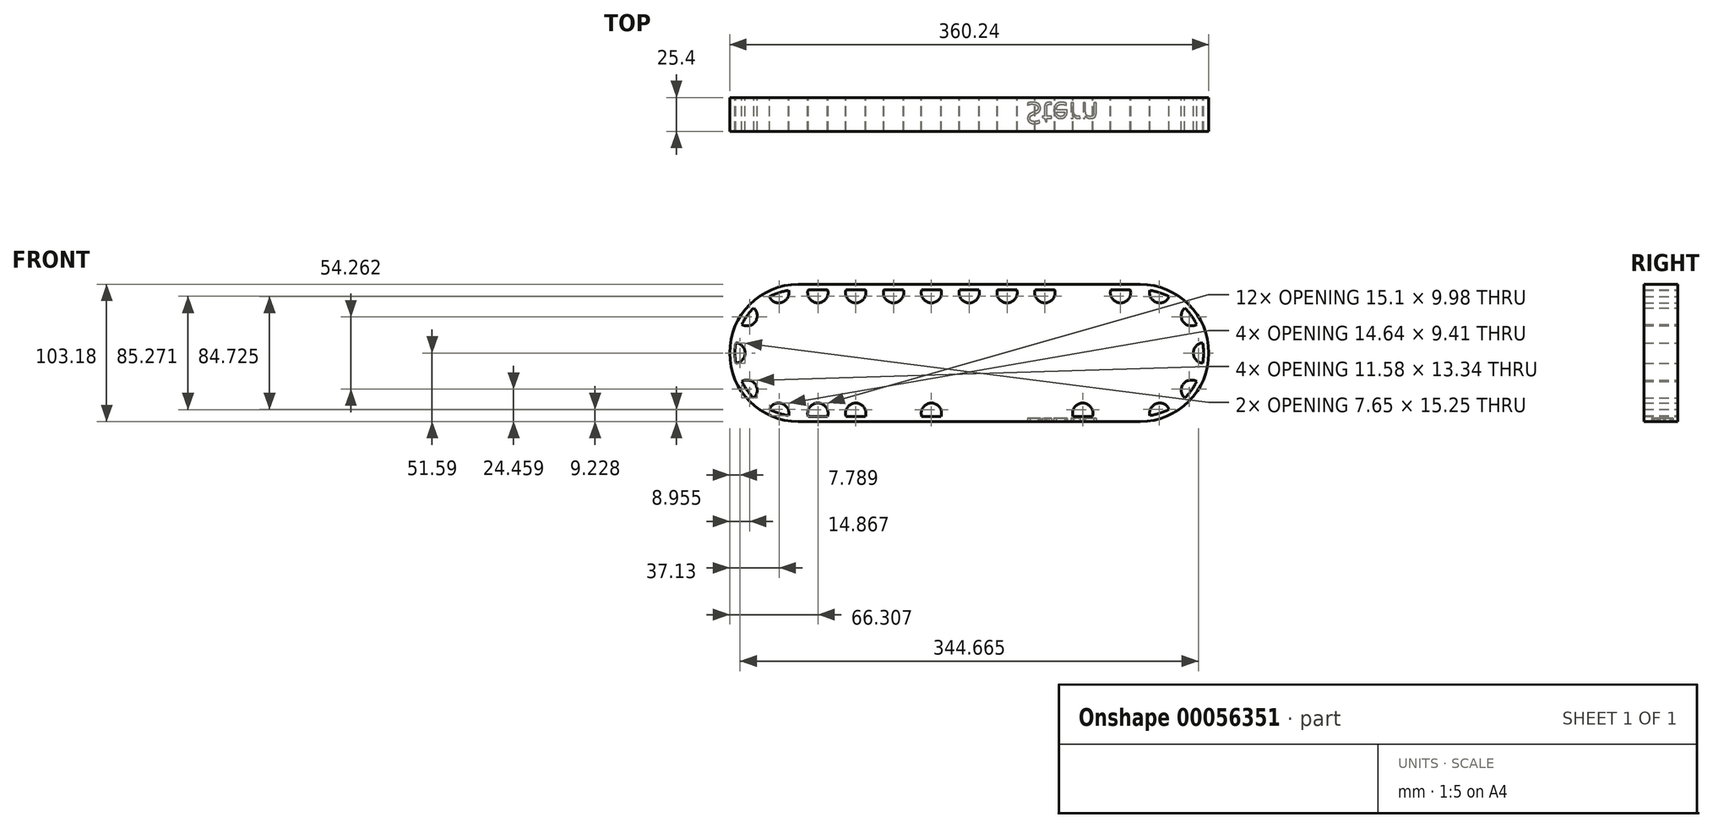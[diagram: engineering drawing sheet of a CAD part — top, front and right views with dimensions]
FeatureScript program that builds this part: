
annotation { "Feature Type Name" : "Feature", "Feature Type Description" : "" }
export const myFeature = defineFeature(function(context is Context, id is Id, definition is map)
    precondition{}
    {
        {
            var Q0;
            Q0=qCreatedBy(makeId("Front.planeOp"),FACE);
            var sketch = newSketch(context, id + "F0", { "sketchPlane" : qUnion([Q0])});
            skCircle(sketch, "E0", {"center": v(0, 0) * mm, "radius": 9.53 * mm});
            skCircle(sketch, "E1", {"center": v(0, 0) * mm, "radius": 15.88 * mm, "construction": true});
            skArc(sketch, "E2", {"start": v(15.06, 35) * mm, "mid": v(11.77, 36.24) * mm, "end": v(8.38, 37.17) * mm});
            skCircle(sketch, "E3", {"center": v(0, 0) * mm, "radius": 25.4 * mm});
            skArc(sketch, "E4", {"start": v(6.62, 47.16) * mm, "mid": v(0, 47.63) * mm, "end": v(-6.62, 47.16) * mm});
            skLineSegment(sketch, "E5", {"start": v(-6.62, 47.16) * mm, "end": v(-8.38, 37.17) * mm});
            skLineSegment(sketch, "E6", {"start": v(-8.38, 37.17) * mm, "end": v(8.38, 37.17) * mm, "construction": true});
            skLineSegment(sketch, "E7", {"start": v(8.38, 37.17) * mm, "end": v(6.62, 47.16) * mm});
            skLineSegment(sketch, "E8", {"start": v(0, 37.17) * mm, "end": v(0, 47.63) * mm, "construction": true});
            skPoint(sketch, "E8.endSnap0", {"position": v(0, 37.17) * mm});
            skArc(sketch, "E9.1.0", {"start": v(-22.36, 42.05) * mm, "mid": v(-28, 38.53) * mm, "end": v(-33.08, 34.26) * mm});
            skLineSegment(sketch, "E9.1.1", {"start": v(-33.08, 34.26) * mm, "end": v(-28.63, 25.14) * mm});
            skLineSegment(sketch, "E9.1.2", {"start": v(-15.06, 35) * mm, "end": v(-22.36, 42.05) * mm});
            skLineSegment(sketch, "E9.1.3", {"start": v(-28.63, 25.14) * mm, "end": v(-21.85, 30.07) * mm, "construction": true});
            skLineSegment(sketch, "E9.1.4", {"start": v(-21.85, 30.07) * mm, "end": v(-28, 38.53) * mm, "construction": true});
            skArc(sketch, "E9.2.0", {"start": v(-42.8, 20.87) * mm, "mid": v(-45.3, 14.72) * mm, "end": v(-46.9, 8.28) * mm});
            skLineSegment(sketch, "E9.2.1", {"start": v(-46.9, 8.28) * mm, "end": v(-37.94, 3.51) * mm});
            skLineSegment(sketch, "E9.2.2", {"start": v(-32.76, 19.46) * mm, "end": v(-42.8, 20.87) * mm});
            skLineSegment(sketch, "E9.2.3", {"start": v(-37.94, 3.51) * mm, "end": v(-32.76, 19.46) * mm, "construction": true});
            skLineSegment(sketch, "E9.2.4", {"start": v(-35.35, 11.48) * mm, "end": v(-45.3, 14.72) * mm, "construction": true});
            skArc(sketch, "E9.3.0", {"start": v(-46.9, -8.28) * mm, "mid": v(-45.3, -14.72) * mm, "end": v(-42.8, -20.87) * mm});
            skLineSegment(sketch, "E9.3.1", {"start": v(-42.8, -20.87) * mm, "end": v(-32.76, -19.46) * mm});
            skLineSegment(sketch, "E9.3.2", {"start": v(-37.94, -3.51) * mm, "end": v(-46.9, -8.28) * mm});
            skLineSegment(sketch, "E9.3.3", {"start": v(-32.76, -19.46) * mm, "end": v(-37.94, -3.51) * mm, "construction": true});
            skLineSegment(sketch, "E9.3.4", {"start": v(-35.35, -11.48) * mm, "end": v(-45.3, -14.72) * mm, "construction": true});
            skArc(sketch, "E9.4.0", {"start": v(-33.08, -34.26) * mm, "mid": v(-28, -38.53) * mm, "end": v(-22.36, -42.05) * mm});
            skLineSegment(sketch, "E9.4.1", {"start": v(-22.36, -42.05) * mm, "end": v(-15.06, -35) * mm});
            skLineSegment(sketch, "E9.4.2", {"start": v(-28.63, -25.14) * mm, "end": v(-33.08, -34.26) * mm});
            skLineSegment(sketch, "E9.4.3", {"start": v(-15.06, -35) * mm, "end": v(-28.63, -25.14) * mm, "construction": true});
            skLineSegment(sketch, "E9.4.4", {"start": v(-21.85, -30.07) * mm, "end": v(-28, -38.53) * mm, "construction": true});
            skArc(sketch, "E9.5.0", {"start": v(-6.62, -47.16) * mm, "mid": v(0, -47.63) * mm, "end": v(6.62, -47.16) * mm});
            skLineSegment(sketch, "E9.5.1", {"start": v(6.62, -47.16) * mm, "end": v(8.38, -37.17) * mm});
            skLineSegment(sketch, "E9.5.2", {"start": v(-8.38, -37.17) * mm, "end": v(-6.62, -47.16) * mm});
            skLineSegment(sketch, "E9.5.3", {"start": v(8.38, -37.17) * mm, "end": v(-8.38, -37.17) * mm, "construction": true});
            skLineSegment(sketch, "E9.5.4", {"start": v(0, -37.17) * mm, "end": v(0, -47.63) * mm, "construction": true});
            skArc(sketch, "E9.6.0", {"start": v(22.36, -42.05) * mm, "mid": v(28, -38.53) * mm, "end": v(33.08, -34.26) * mm});
            skLineSegment(sketch, "E9.6.1", {"start": v(33.08, -34.26) * mm, "end": v(28.63, -25.14) * mm});
            skLineSegment(sketch, "E9.6.2", {"start": v(15.06, -35) * mm, "end": v(22.36, -42.05) * mm});
            skLineSegment(sketch, "E9.6.3", {"start": v(28.63, -25.14) * mm, "end": v(15.06, -35) * mm, "construction": true});
            skLineSegment(sketch, "E9.6.4", {"start": v(21.85, -30.07) * mm, "end": v(28, -38.53) * mm, "construction": true});
            skArc(sketch, "E9.7.0", {"start": v(42.8, -20.87) * mm, "mid": v(45.3, -14.72) * mm, "end": v(46.9, -8.28) * mm});
            skLineSegment(sketch, "E9.7.1", {"start": v(46.9, -8.28) * mm, "end": v(37.94, -3.51) * mm});
            skLineSegment(sketch, "E9.7.2", {"start": v(32.76, -19.46) * mm, "end": v(42.8, -20.87) * mm});
            skLineSegment(sketch, "E9.7.3", {"start": v(37.94, -3.51) * mm, "end": v(32.76, -19.46) * mm, "construction": true});
            skLineSegment(sketch, "E9.7.4", {"start": v(35.35, -11.48) * mm, "end": v(45.3, -14.72) * mm, "construction": true});
            skArc(sketch, "E9.8.0", {"start": v(46.9, 8.28) * mm, "mid": v(45.3, 14.72) * mm, "end": v(42.8, 20.87) * mm});
            skLineSegment(sketch, "E9.8.1", {"start": v(42.8, 20.87) * mm, "end": v(32.76, 19.46) * mm});
            skLineSegment(sketch, "E9.8.2", {"start": v(37.94, 3.51) * mm, "end": v(46.9, 8.28) * mm});
            skLineSegment(sketch, "E9.8.3", {"start": v(32.76, 19.46) * mm, "end": v(37.94, 3.51) * mm, "construction": true});
            skLineSegment(sketch, "E9.8.4", {"start": v(35.35, 11.48) * mm, "end": v(45.3, 14.72) * mm, "construction": true});
            skArc(sketch, "E9.9.0", {"start": v(33.08, 34.26) * mm, "mid": v(28, 38.53) * mm, "end": v(22.36, 42.05) * mm});
            skLineSegment(sketch, "E9.9.1", {"start": v(22.36, 42.05) * mm, "end": v(15.06, 35) * mm});
            skLineSegment(sketch, "E9.9.2", {"start": v(28.63, 25.14) * mm, "end": v(33.08, 34.26) * mm});
            skLineSegment(sketch, "E9.9.3", {"start": v(15.06, 35) * mm, "end": v(28.63, 25.14) * mm, "construction": true});
            skLineSegment(sketch, "E9.9.4", {"start": v(21.85, 30.07) * mm, "end": v(28, 38.53) * mm, "construction": true});
            skArc(sketch, "E10.trimOffspring", {"start": v(37.94, -3.51) * mm, "mid": v(38.1, 0) * mm, "end": v(37.94, 3.51) * mm});
            skArc(sketch, "E11.trimOffspring", {"start": v(28.63, -25.14) * mm, "mid": v(30.82, -22.4) * mm, "end": v(32.76, -19.46) * mm});
            skArc(sketch, "E12.trimOffspring", {"start": v(8.38, -37.17) * mm, "mid": v(11.77, -36.24) * mm, "end": v(15.06, -35) * mm});
            skArc(sketch, "E13.trimOffspring", {"start": v(-15.06, -35) * mm, "mid": v(-11.77, -36.24) * mm, "end": v(-8.38, -37.17) * mm});
            skArc(sketch, "E14.trimOffspring", {"start": v(-32.76, -19.46) * mm, "mid": v(-30.82, -22.4) * mm, "end": v(-28.63, -25.14) * mm});
            skArc(sketch, "E15.trimOffspring", {"start": v(-37.94, 3.51) * mm, "mid": v(-38.1, 0) * mm, "end": v(-37.94, -3.51) * mm});
            skArc(sketch, "E16.trimOffspring", {"start": v(-8.38, 37.17) * mm, "mid": v(-11.77, 36.24) * mm, "end": v(-15.06, 35) * mm});
            skArc(sketch, "E17.trimOffspring", {"start": v(-28.63, 25.14) * mm, "mid": v(-29.76, 23.8) * mm, "end": v(-30.82, 22.4) * mm});
            skArc(sketch, "E18", {"start": v(-30.82, 22.4) * mm, "mid": v(-31.82, 20.95) * mm, "end": v(-32.76, 19.46) * mm});
            skArc(sketch, "E19.trimOffspring", {"start": v(32.76, 19.46) * mm, "mid": v(30.82, 22.4) * mm, "end": v(28.63, 25.14) * mm});
            skLineSegment(sketch, "E20", {"start": v(-21.85, 30.07) * mm, "end": v(-15.06, 35) * mm, "construction": true});
            skPoint(sketch, "E21.endSnap0", {"position": v(-30.82, 22.4) * mm});
            skLineSegment(sketch, "E22", {"start": v(0, 9.53) * mm, "end": v(0, 15.88) * mm, "construction": true});
            skLineSegment(sketch, "E23", {"start": v(0, 9.53) * mm, "end": v(0, 9.53) * mm});
            skLineSegment(sketch, "E24", {"start": v(-3.98, 8.66) * mm, "end": v(-3.98, 15.37) * mm, "construction": true});
            skLineSegment(sketch, "E25", {"start": v(3.98, 8.66) * mm, "end": v(3.98, 15.37) * mm, "construction": true});
            skLineSegment(sketch, "E26", {"start": v(3.98, 15.37) * mm, "end": v(3.98, 8.66) * mm, "construction": true});
            skLineSegment(sketch, "E27", {"start": v(3.98, 8.66) * mm, "end": v(-3.98, 8.66) * mm, "construction": true});
            skLineSegment(sketch, "E28", {"start": v(-3.98, 8.66) * mm, "end": v(-3.98, 25.09) * mm, "construction": true});
            skLineSegment(sketch, "E29", {"start": v(3.98, 8.66) * mm, "end": v(3.98, 25.09) * mm, "construction": true});
            skLineSegment(sketch, "E30", {"start": v(0, 9.53) * mm, "end": v(0, 25.4) * mm, "construction": true});
            skPoint(sketch, "E30.endSnap0", {"position": v(0, 12.7) * mm});
            skLineSegment(sketch, "E31.1.0", {"start": v(-9.48, -0.89) * mm, "end": v(-23.71, -9.1) * mm, "construction": true});
            skLineSegment(sketch, "E31.1.1", {"start": v(-8.25, -4.76) * mm, "end": v(-22, -12.7) * mm, "construction": true});
            skLineSegment(sketch, "E31.1.2", {"start": v(-5.5, -7.77) * mm, "end": v(-19.74, -15.99) * mm, "construction": true});
            skLineSegment(sketch, "E31.1.3", {"start": v(-9.48, -0.89) * mm, "end": v(-5.5, -7.77) * mm, "construction": true});
            skLineSegment(sketch, "E31.2.0", {"start": v(5.5, -7.77) * mm, "end": v(19.74, -15.99) * mm, "construction": true});
            skLineSegment(sketch, "E31.2.1", {"start": v(8.25, -4.76) * mm, "end": v(22, -12.7) * mm, "construction": true});
            skLineSegment(sketch, "E31.2.2", {"start": v(9.48, -0.89) * mm, "end": v(23.71, -9.1) * mm, "construction": true});
            skLineSegment(sketch, "E31.2.3", {"start": v(5.5, -7.77) * mm, "end": v(9.48, -0.89) * mm, "construction": true});
            skSolve(sketch);
        }
        {
            var Q0;
            Q0=qCreatedBy(makeId("Front.planeOp"),FACE);
            var sketch = newSketch(context, id + "F1", { "sketchPlane" : qUnion([Q0])});
            skArc(sketch, "E32", {"start": v(22.36, 42.05) * mm, "mid": v(22.07, 42.2) * mm, "end": v(21.78, 42.35) * mm});
            skLineSegment(sketch, "E33.0", {"start": v(22.36, 42.05) * mm, "end": v(15.06, 35) * mm, "construction": true});
            skLineSegment(sketch, "E33.1", {"start": v(8.38, 37.17) * mm, "end": v(6.62, 47.16) * mm, "construction": true});
            skLineSegment(sketch, "E33.2", {"start": v(-6.62, 47.16) * mm, "end": v(-8.38, 37.17) * mm, "construction": true});
            skLineSegment(sketch, "E33.3", {"start": v(-15.06, 35) * mm, "end": v(-22.36, 42.05) * mm, "construction": true});
            skLineSegment(sketch, "E33.4", {"start": v(-33.08, 34.26) * mm, "end": v(-28.63, 25.14) * mm, "construction": true});
            skLineSegment(sketch, "E33.5", {"start": v(-32.76, 19.46) * mm, "end": v(-42.8, 20.87) * mm, "construction": true});
            skLineSegment(sketch, "E33.6", {"start": v(-46.9, 8.28) * mm, "end": v(-37.94, 3.51) * mm, "construction": true});
            skLineSegment(sketch, "E33.7", {"start": v(-37.94, -3.51) * mm, "end": v(-46.9, -8.28) * mm, "construction": true});
            skLineSegment(sketch, "E33.8", {"start": v(-42.8, -20.87) * mm, "end": v(-32.76, -19.46) * mm, "construction": true});
            skCircle(sketch, "E34", {"center": v(-14.72, 45.3) * mm, "radius": 7.65 * mm});
            skCircle(sketch, "E35", {"center": v(-38.53, 28) * mm, "radius": 7.65 * mm});
            skCircle(sketch, "E36", {"center": v(-47.63, 0) * mm, "radius": 7.65 * mm});
            skCircle(sketch, "E37", {"center": v(-38.53, -28) * mm, "radius": 7.65 * mm});
            skCircle(sketch, "E38.MirrorC", {"center": v(14.72, 45.3) * mm, "radius": 7.65 * mm});
            skLineSegment(sketch, "E39", {"start": v(-14.72, 45.3) * mm, "end": v(14.72, 45.3) * mm, "construction": true});
            skArc(sketch, "E40.trimOffspring", {"start": v(-22.36, 42.05) * mm, "mid": v(-42.05, -22.36) * mm, "end": v(22.36, -42.05) * mm});
            skArc(sketch, "E41.trimOffspring", {"start": v(7.28, 47.07) * mm, "mid": v(0.33, 47.62) * mm, "end": v(-6.62, 47.16) * mm});
            skLineSegment(sketch, "E42", {"start": v(14.72, 45.3) * mm, "end": v(43.17, 45.3) * mm, "construction": true});
            skLineSegment(sketch, "E43", {"start": v(43.17, 45.3) * mm, "end": v(71.62, 45.3) * mm, "construction": true});
            skLineSegment(sketch, "E44", {"start": v(71.62, 45.3) * mm, "end": v(100.08, 45.3) * mm, "construction": true});
            skLineSegment(sketch, "E45", {"start": v(100.08, 45.3) * mm, "end": v(128.53, 45.3) * mm, "construction": true});
            skCircle(sketch, "E46", {"center": v(43.17, 45.3) * mm, "radius": 7.65 * mm});
            skCircle(sketch, "E47", {"center": v(71.62, 45.3) * mm, "radius": 7.65 * mm});
            skCircle(sketch, "E48", {"center": v(100.08, 45.3) * mm, "radius": 7.65 * mm});
            skCircle(sketch, "E49", {"center": v(128.53, 45.3) * mm, "radius": 7.65 * mm});
            skPoint(sketch, "E50", {"position": v(35.52, 45.3) * mm});
            skPoint(sketch, "E51", {"position": v(22.37, 45.3) * mm});
            skPoint(sketch, "E51.positionSnap0", {"position": v(28.94, 45.3) * mm});
            skLineSegment(sketch, "E52", {"start": v(0, 0) * mm, "end": v(128.53, 0) * mm, "construction": true});
            skLineSegment(sketch, "E53", {"start": v(128.53, 0) * mm, "end": v(128.53, 45.3) * mm, "construction": true});
            skCircle(sketch, "E54.MirrorC", {"center": v(43.17, -45.3) * mm, "radius": 7.65 * mm});
            skCircle(sketch, "E55.MirrorC", {"center": v(71.62, -45.3) * mm, "radius": 7.65 * mm});
            skCircle(sketch, "E56.MirrorC", {"center": v(100.08, -45.3) * mm, "radius": 7.65 * mm});
            skCircle(sketch, "E57.MirrorC", {"center": v(128.53, -45.3) * mm, "radius": 7.65 * mm});
            skCircle(sketch, "E58.MirrorC", {"center": v(14.72, -45.3) * mm, "radius": 7.65 * mm});
            skCircle(sketch, "E59.MirrorC", {"center": v(-14.72, -45.3) * mm, "radius": 7.65 * mm});
            skCircle(sketch, "E60.MirrorC", {"center": v(156.99, 45.3) * mm, "radius": 7.65 * mm});
            skCircle(sketch, "E61.MirrorC", {"center": v(185.44, 45.3) * mm, "radius": 7.65 * mm});
            skCircle(sketch, "E62.MirrorC", {"center": v(213.9, 45.3) * mm, "radius": 7.65 * mm});
            skCircle(sketch, "E63.MirrorC", {"center": v(242.35, 45.3) * mm, "radius": 7.65 * mm});
            skCircle(sketch, "E64.MirrorC", {"center": v(271.78, 45.3) * mm, "radius": 7.65 * mm});
            skCircle(sketch, "E65.MirrorC", {"center": v(295.6, 28) * mm, "radius": 7.65 * mm});
            skCircle(sketch, "E66.MirrorC", {"center": v(304.69, 0) * mm, "radius": 7.65 * mm});
            skCircle(sketch, "E67.MirrorC", {"center": v(295.6, -28) * mm, "radius": 7.65 * mm});
            skCircle(sketch, "E68.MirrorC", {"center": v(271.78, -45.3) * mm, "radius": 7.65 * mm});
            skCircle(sketch, "E69.MirrorC", {"center": v(242.35, -45.3) * mm, "radius": 7.65 * mm});
            skCircle(sketch, "E70.MirrorC", {"center": v(213.9, -45.3) * mm, "radius": 7.65 * mm});
            skCircle(sketch, "E71.MirrorC", {"center": v(185.44, -45.3) * mm, "radius": 7.65 * mm});
            skCircle(sketch, "E72.MirrorC", {"center": v(156.99, -45.3) * mm, "radius": 7.65 * mm});
            skSolve(sketch);
        }
        {
            var Q0;
            Q0=qCreatedBy(makeId("Front.planeOp"),FACE);
            var sketch = newSketch(context, id + "F2", { "sketchPlane" : qUnion([Q0])});
            skArc(sketch, "E73", {"start": v(0, -47.63) * mm, "mid": v(-47.63, 0) * mm, "end": v(0, 47.63) * mm});
            skLineSegment(sketch, "E74", {"start": v(0, 47.63) * mm, "end": v(257.06, 47.63) * mm});
            skLineSegment(sketch, "E75", {"start": v(0, -47.63) * mm, "end": v(257.06, -47.62) * mm});
            skLineSegment(sketch, "E76.0", {"start": v(128.53, 0) * mm, "end": v(128.53, 45.3) * mm, "construction": true});
            skLineSegment(sketch, "E77.0", {"start": v(0, 0) * mm, "end": v(128.53, 0) * mm, "construction": true});
            skLineSegment(sketch, "E78.MirrorCS", {"start": v(257.06, 0) * mm, "end": v(128.53, 0) * mm, "construction": true});
            skArc(sketch, "E79", {"start": v(257.06, 47.63) * mm, "mid": v(304.69, 0) * mm, "end": v(257.06, -47.63) * mm});
            skLineSegment(sketch, "E80.0", {"start": v(0, 51.59) * mm, "end": v(257.06, 51.59) * mm});
            skArc(sketch, "E80.1", {"start": v(0, -51.59) * mm, "mid": v(-51.59, 0) * mm, "end": v(0, 51.59) * mm});
            skLineSegment(sketch, "E80.2", {"start": v(0, -51.59) * mm, "end": v(257.06, -51.59) * mm});
            skArc(sketch, "E80.3", {"start": v(257.06, 51.59) * mm, "mid": v(308.65, 0) * mm, "end": v(257.06, -51.59) * mm});
            skArc(sketch, "E81.0", {"start": v(19.06, 51.59) * mm, "mid": v(14.72, 37.65) * mm, "end": v(10.37, 51.59) * mm});
            skArc(sketch, "E81.1", {"start": v(-22.26, 46.54) * mm, "mid": v(-12.35, 38.02) * mm, "end": v(-9.34, 50.73) * mm});
            skArc(sketch, "E81.2", {"start": v(38.82, 51.59) * mm, "mid": v(43.17, 37.65) * mm, "end": v(47.52, 51.59) * mm});
            skArc(sketch, "E81.3", {"start": v(67.28, 51.59) * mm, "mid": v(71.62, 37.65) * mm, "end": v(75.97, 51.59) * mm});
            skArc(sketch, "E81.4", {"start": v(95.73, 51.59) * mm, "mid": v(100.08, 37.65) * mm, "end": v(104.42, 51.59) * mm});
            skArc(sketch, "E81.5", {"start": v(132.88, 51.59) * mm, "mid": v(128.53, 37.65) * mm, "end": v(124.19, 51.59) * mm});
            skArc(sketch, "E81.6", {"start": v(161.33, 51.59) * mm, "mid": v(159.45, 38.05) * mm, "end": v(149.7, 47.63) * mm});
            skArc(sketch, "E81.7", {"start": v(189.79, 51.59) * mm, "mid": v(185.44, 37.65) * mm, "end": v(181.1, 51.59) * mm});
            skArc(sketch, "E81.8", {"start": v(218.24, 51.59) * mm, "mid": v(213.9, 37.65) * mm, "end": v(209.55, 51.59) * mm});
            skArc(sketch, "E81.9", {"start": v(238, 51.59) * mm, "mid": v(242.35, 37.65) * mm, "end": v(246.7, 51.59) * mm});
            skArc(sketch, "E81.10", {"start": v(218.24, -51.59) * mm, "mid": v(213.9, -37.65) * mm, "end": v(209.55, -51.59) * mm});
            skArc(sketch, "E81.11", {"start": v(189.79, -51.59) * mm, "mid": v(185.44, -37.65) * mm, "end": v(181.1, -51.59) * mm});
            skArc(sketch, "E81.12", {"start": v(161.33, -51.59) * mm, "mid": v(156.99, -37.65) * mm, "end": v(152.64, -51.59) * mm});
            skArc(sketch, "E81.13", {"start": v(124.19, -51.59) * mm, "mid": v(128.53, -37.65) * mm, "end": v(132.88, -51.59) * mm});
            skArc(sketch, "E81.14", {"start": v(95.73, -51.59) * mm, "mid": v(100.08, -37.65) * mm, "end": v(104.42, -51.59) * mm});
            skArc(sketch, "E81.15", {"start": v(67.28, -51.59) * mm, "mid": v(71.62, -37.65) * mm, "end": v(75.97, -51.59) * mm});
            skArc(sketch, "E81.16", {"start": v(38.82, -51.59) * mm, "mid": v(43.17, -37.65) * mm, "end": v(47.52, -51.59) * mm});
            skArc(sketch, "E81.17", {"start": v(-45.36, 24.56) * mm, "mid": v(-32.34, 23.5) * mm, "end": v(-37.38, 35.55) * mm});
            skArc(sketch, "E81.18", {"start": v(-51.14, -6.8) * mm, "mid": v(-39.98, 0) * mm, "end": v(-51.14, 6.8) * mm});
            skArc(sketch, "E81.19", {"start": v(-45.36, -24.56) * mm, "mid": v(-32.34, -23.5) * mm, "end": v(-37.38, -35.55) * mm});
            skArc(sketch, "E81.20", {"start": v(-22.26, -46.54) * mm, "mid": v(-12.35, -38.02) * mm, "end": v(-9.34, -50.73) * mm});
            skArc(sketch, "E81.21", {"start": v(19.06, -51.59) * mm, "mid": v(14.72, -37.65) * mm, "end": v(10.37, -51.59) * mm});
            skArc(sketch, "E81.22", {"start": v(238, -51.59) * mm, "mid": v(242.35, -37.65) * mm, "end": v(246.7, -51.59) * mm});
            skArc(sketch, "E81.23", {"start": v(279.33, -46.54) * mm, "mid": v(269.42, -38.02) * mm, "end": v(266.4, -50.73) * mm});
            skArc(sketch, "E81.24", {"start": v(302.43, -24.56) * mm, "mid": v(289.4, -23.5) * mm, "end": v(294.44, -35.55) * mm});
            skArc(sketch, "E81.25", {"start": v(308.2, -6.8) * mm, "mid": v(297.04, 0) * mm, "end": v(308.2, 6.8) * mm});
            skArc(sketch, "E81.26", {"start": v(302.43, 24.56) * mm, "mid": v(289.4, 23.5) * mm, "end": v(294.44, 35.55) * mm});
            skArc(sketch, "E81.27", {"start": v(279.33, 46.54) * mm, "mid": v(269.42, 38.02) * mm, "end": v(266.4, 50.73) * mm});
            skSolve(sketch);
        }
        {
            var Q0;
            Q0 = qSketchRegion(id + "F2", true);
            var Q1;
            {var subQ0=sQuery(id+"F2.wireOp",EDGE,"E81.20");var subQ1=sQuery(id+"F2.wireOp",EDGE,"E73");var subQ2=makeQuery(id+"F2.imprint","INTERSECT",VERTEX,{"disambiguationData":[OD(0.0)],"derivedFrom":[subQ1,subQ0]});Q1=makeQuery(id+"F2.imprint","IMPRINT",FACE,{"disambiguationData":[TD([[makeQuery(id+"F2.imprint","IMPRINT",EDGE,{"disambiguationData":[TD([[subQ2,-1.0]])],"derivedFrom":subQ1}),-1.0]])]});}
            var Q2;
            {var subQ0=sQuery(id+"F2.wireOp",EDGE,"E81.21");var subQ1=sQuery(id+"F2.wireOp",EDGE,"E75");var subQ2=makeQuery(id+"F2.imprint","INTERSECT",VERTEX,{"disambiguationData":[OD(0.0)],"derivedFrom":[subQ1,subQ0]});Q2=makeQuery(id+"F2.imprint","IMPRINT",FACE,{"disambiguationData":[TD([[makeQuery(id+"F2.imprint","IMPRINT",EDGE,{"disambiguationData":[TD([[subQ2,-1.0]])],"derivedFrom":subQ1}),1.0]])]});}
            var Q3;
            {var subQ0=sQuery(id+"F2.wireOp",EDGE,"E81.16");var subQ1=sQuery(id+"F2.wireOp",EDGE,"E75");var subQ2=makeQuery(id+"F2.imprint","INTERSECT",VERTEX,{"disambiguationData":[OD(0.0)],"derivedFrom":[subQ1,subQ0]});Q3=makeQuery(id+"F2.imprint","IMPRINT",FACE,{"disambiguationData":[TD([[makeQuery(id+"F2.imprint","IMPRINT",EDGE,{"disambiguationData":[TD([[subQ2,-1.0]])],"derivedFrom":subQ1}),1.0]])]});}
            var Q4;
            {var subQ0=sQuery(id+"F2.wireOp",EDGE,"E81.15");var subQ1=sQuery(id+"F2.wireOp",EDGE,"E75");var subQ2=makeQuery(id+"F2.imprint","INTERSECT",VERTEX,{"disambiguationData":[OD(0.0)],"derivedFrom":[subQ1,subQ0]});Q4=makeQuery(id+"F2.imprint","IMPRINT",FACE,{"disambiguationData":[TD([[makeQuery(id+"F2.imprint","IMPRINT",EDGE,{"disambiguationData":[TD([[subQ2,-1.0]])],"derivedFrom":subQ1}),1.0]])]});}
            var Q5;
            {var subQ0=sQuery(id+"F2.wireOp",EDGE,"E81.14");var subQ1=sQuery(id+"F2.wireOp",EDGE,"E75");var subQ2=makeQuery(id+"F2.imprint","INTERSECT",VERTEX,{"disambiguationData":[OD(0.0)],"derivedFrom":[subQ1,subQ0]});Q5=makeQuery(id+"F2.imprint","IMPRINT",FACE,{"disambiguationData":[TD([[makeQuery(id+"F2.imprint","IMPRINT",EDGE,{"disambiguationData":[TD([[subQ2,-1.0]])],"derivedFrom":subQ1}),1.0]])]});}
            var Q6;
            {var subQ0=sQuery(id+"F2.wireOp",EDGE,"E81.13");var subQ1=sQuery(id+"F2.wireOp",EDGE,"E75");var subQ2=makeQuery(id+"F2.imprint","INTERSECT",VERTEX,{"disambiguationData":[OD(0.0)],"derivedFrom":[subQ1,subQ0]});Q6=makeQuery(id+"F2.imprint","IMPRINT",FACE,{"disambiguationData":[TD([[makeQuery(id+"F2.imprint","IMPRINT",EDGE,{"disambiguationData":[TD([[subQ2,-1.0]])],"derivedFrom":subQ1}),1.0]])]});}
            var Q7;
            {var subQ0=sQuery(id+"F2.wireOp",EDGE,"E81.12");var subQ1=sQuery(id+"F2.wireOp",EDGE,"E75");var subQ2=makeQuery(id+"F2.imprint","INTERSECT",VERTEX,{"disambiguationData":[OD(0.0)],"derivedFrom":[subQ1,subQ0]});Q7=makeQuery(id+"F2.imprint","IMPRINT",FACE,{"disambiguationData":[TD([[makeQuery(id+"F2.imprint","IMPRINT",EDGE,{"disambiguationData":[TD([[subQ2,-1.0]])],"derivedFrom":subQ1}),1.0]])]});}
            var Q8;
            {var subQ0=sQuery(id+"F2.wireOp",EDGE,"E81.11");var subQ1=sQuery(id+"F2.wireOp",EDGE,"E75");var subQ2=makeQuery(id+"F2.imprint","INTERSECT",VERTEX,{"disambiguationData":[OD(0.0)],"derivedFrom":[subQ1,subQ0]});Q8=makeQuery(id+"F2.imprint","IMPRINT",FACE,{"disambiguationData":[TD([[makeQuery(id+"F2.imprint","IMPRINT",EDGE,{"disambiguationData":[TD([[subQ2,-1.0]])],"derivedFrom":subQ1}),1.0]])]});}
            var Q9;
            {var subQ0=sQuery(id+"F2.wireOp",EDGE,"E81.10");var subQ1=sQuery(id+"F2.wireOp",EDGE,"E75");var subQ2=makeQuery(id+"F2.imprint","INTERSECT",VERTEX,{"disambiguationData":[OD(0.0)],"derivedFrom":[subQ1,subQ0]});Q9=makeQuery(id+"F2.imprint","IMPRINT",FACE,{"disambiguationData":[TD([[makeQuery(id+"F2.imprint","IMPRINT",EDGE,{"disambiguationData":[TD([[subQ2,-1.0]])],"derivedFrom":subQ1}),1.0]])]});}
            var Q10;
            {var subQ0=sQuery(id+"F2.wireOp",EDGE,"E81.22");var subQ1=sQuery(id+"F2.wireOp",EDGE,"E75");var subQ2=makeQuery(id+"F2.imprint","INTERSECT",VERTEX,{"disambiguationData":[OD(0.0)],"derivedFrom":[subQ1,subQ0]});Q10=makeQuery(id+"F2.imprint","IMPRINT",FACE,{"disambiguationData":[TD([[makeQuery(id+"F2.imprint","IMPRINT",EDGE,{"disambiguationData":[TD([[subQ2,-1.0]])],"derivedFrom":subQ1}),1.0]])]});}
            var Q11;
            {var subQ0=sQuery(id+"F2.wireOp",EDGE,"E81.23");var subQ1=sQuery(id+"F2.wireOp",EDGE,"E79");var subQ2=makeQuery(id+"F2.imprint","INTERSECT",VERTEX,{"disambiguationData":[OD(0.0)],"derivedFrom":[subQ1,subQ0]});Q11=makeQuery(id+"F2.imprint","IMPRINT",FACE,{"disambiguationData":[TD([[makeQuery(id+"F2.imprint","IMPRINT",EDGE,{"disambiguationData":[TD([[subQ2,-1.0]])],"derivedFrom":subQ1}),-1.0]])]});}
            var Q12;
            {var subQ0=sQuery(id+"F2.wireOp",EDGE,"E81.0");var subQ1=sQuery(id+"F2.wireOp",EDGE,"E74");var subQ2=makeQuery(id+"F2.imprint","INTERSECT",VERTEX,{"disambiguationData":[OD(0.0)],"derivedFrom":[subQ1,subQ0]});Q12=makeQuery(id+"F2.imprint","IMPRINT",FACE,{"disambiguationData":[TD([[makeQuery(id+"F2.imprint","IMPRINT",EDGE,{"disambiguationData":[TD([[subQ2,-1.0]])],"derivedFrom":subQ1}),-1.0]])]});}
            var Q13;
            {var subQ0=sQuery(id+"F2.wireOp",EDGE,"E81.1");var subQ1=sQuery(id+"F2.wireOp",EDGE,"E73");var subQ2=makeQuery(id+"F2.imprint","INTERSECT",VERTEX,{"disambiguationData":[OD(0.0)],"derivedFrom":[subQ1,subQ0]});Q13=makeQuery(id+"F2.imprint","IMPRINT",FACE,{"disambiguationData":[TD([[makeQuery(id+"F2.imprint","IMPRINT",EDGE,{"disambiguationData":[TD([[subQ2,-1.0]])],"derivedFrom":subQ1}),-1.0]])]});}
            var Q14;
            {var subQ0=sQuery(id+"F2.wireOp",EDGE,"E81.17");var subQ1=sQuery(id+"F2.wireOp",EDGE,"E73");var subQ2=makeQuery(id+"F2.imprint","INTERSECT",VERTEX,{"disambiguationData":[OD(0.0)],"derivedFrom":[subQ1,subQ0]});Q14=makeQuery(id+"F2.imprint","IMPRINT",FACE,{"disambiguationData":[TD([[makeQuery(id+"F2.imprint","IMPRINT",EDGE,{"disambiguationData":[TD([[subQ2,-1.0]])],"derivedFrom":subQ1}),-1.0]])]});}
            var Q15;
            {var subQ0=sQuery(id+"F2.wireOp",EDGE,"E81.18");var subQ1=sQuery(id+"F2.wireOp",EDGE,"E73");var subQ2=makeQuery(id+"F2.imprint","INTERSECT",VERTEX,{"disambiguationData":[OD(0.0)],"derivedFrom":[subQ1,subQ0]});Q15=makeQuery(id+"F2.imprint","IMPRINT",FACE,{"disambiguationData":[TD([[makeQuery(id+"F2.imprint","IMPRINT",EDGE,{"disambiguationData":[TD([[subQ2,-1.0]])],"derivedFrom":subQ1}),-1.0]])]});}
            var Q16;
            {var subQ0=sQuery(id+"F2.wireOp",EDGE,"E81.19");var subQ1=sQuery(id+"F2.wireOp",EDGE,"E73");var subQ2=makeQuery(id+"F2.imprint","INTERSECT",VERTEX,{"disambiguationData":[OD(0.0)],"derivedFrom":[subQ1,subQ0]});Q16=makeQuery(id+"F2.imprint","IMPRINT",FACE,{"disambiguationData":[TD([[makeQuery(id+"F2.imprint","IMPRINT",EDGE,{"disambiguationData":[TD([[subQ2,-1.0]])],"derivedFrom":subQ1}),-1.0]])]});}
            var Q17;
            {var subQ0=sQuery(id+"F2.wireOp",EDGE,"E81.2");var subQ1=sQuery(id+"F2.wireOp",EDGE,"E74");var subQ2=makeQuery(id+"F2.imprint","INTERSECT",VERTEX,{"disambiguationData":[OD(0.0)],"derivedFrom":[subQ1,subQ0]});Q17=makeQuery(id+"F2.imprint","IMPRINT",FACE,{"disambiguationData":[TD([[makeQuery(id+"F2.imprint","IMPRINT",EDGE,{"disambiguationData":[TD([[subQ2,-1.0]])],"derivedFrom":subQ1}),-1.0]])]});}
            var Q18;
            {var subQ0=sQuery(id+"F2.wireOp",EDGE,"E81.3");var subQ1=sQuery(id+"F2.wireOp",EDGE,"E74");var subQ2=makeQuery(id+"F2.imprint","INTERSECT",VERTEX,{"disambiguationData":[OD(0.0)],"derivedFrom":[subQ1,subQ0]});Q18=makeQuery(id+"F2.imprint","IMPRINT",FACE,{"disambiguationData":[TD([[makeQuery(id+"F2.imprint","IMPRINT",EDGE,{"disambiguationData":[TD([[subQ2,-1.0]])],"derivedFrom":subQ1}),-1.0]])]});}
            var Q19;
            {var subQ0=sQuery(id+"F2.wireOp",EDGE,"E81.4");var subQ1=sQuery(id+"F2.wireOp",EDGE,"E74");var subQ2=makeQuery(id+"F2.imprint","INTERSECT",VERTEX,{"disambiguationData":[OD(0.0)],"derivedFrom":[subQ1,subQ0]});Q19=makeQuery(id+"F2.imprint","IMPRINT",FACE,{"disambiguationData":[TD([[makeQuery(id+"F2.imprint","IMPRINT",EDGE,{"disambiguationData":[TD([[subQ2,-1.0]])],"derivedFrom":subQ1}),-1.0]])]});}
            var Q20;
            {var subQ0=sQuery(id+"F2.wireOp",EDGE,"E81.5");var subQ1=sQuery(id+"F2.wireOp",EDGE,"E74");var subQ2=makeQuery(id+"F2.imprint","INTERSECT",VERTEX,{"disambiguationData":[OD(0.0)],"derivedFrom":[subQ1,subQ0]});Q20=makeQuery(id+"F2.imprint","IMPRINT",FACE,{"disambiguationData":[TD([[makeQuery(id+"F2.imprint","IMPRINT",EDGE,{"disambiguationData":[TD([[subQ2,-1.0]])],"derivedFrom":subQ1}),-1.0]])]});}
            var Q21;
            {var subQ0=sQuery(id+"F2.wireOp",EDGE,"E81.6");var subQ1=sQuery(id+"F2.wireOp",EDGE,"E74");var subQ2=makeQuery(id+"F2.imprint","INTERSECT",VERTEX,{"disambiguationData":[OD(0.0)],"derivedFrom":[subQ1,subQ0]});Q21=makeQuery(id+"F2.imprint","IMPRINT",FACE,{"disambiguationData":[TD([[makeQuery(id+"F2.imprint","IMPRINT",EDGE,{"disambiguationData":[TD([[subQ2,-1.0]])],"derivedFrom":subQ1}),-1.0]])]});}
            var Q22;
            {var subQ0=sQuery(id+"F2.wireOp",EDGE,"E81.7");var subQ1=sQuery(id+"F2.wireOp",EDGE,"E74");var subQ2=makeQuery(id+"F2.imprint","INTERSECT",VERTEX,{"disambiguationData":[OD(0.0)],"derivedFrom":[subQ1,subQ0]});Q22=makeQuery(id+"F2.imprint","IMPRINT",FACE,{"disambiguationData":[TD([[makeQuery(id+"F2.imprint","IMPRINT",EDGE,{"disambiguationData":[TD([[subQ2,-1.0]])],"derivedFrom":subQ1}),-1.0]])]});}
            var Q23;
            {var subQ0=sQuery(id+"F2.wireOp",EDGE,"E81.8");var subQ1=sQuery(id+"F2.wireOp",EDGE,"E74");var subQ2=makeQuery(id+"F2.imprint","INTERSECT",VERTEX,{"disambiguationData":[OD(0.0)],"derivedFrom":[subQ1,subQ0]});Q23=makeQuery(id+"F2.imprint","IMPRINT",FACE,{"disambiguationData":[TD([[makeQuery(id+"F2.imprint","IMPRINT",EDGE,{"disambiguationData":[TD([[subQ2,-1.0]])],"derivedFrom":subQ1}),-1.0]])]});}
            var Q24;
            {var subQ0=sQuery(id+"F2.wireOp",EDGE,"E81.9");var subQ1=sQuery(id+"F2.wireOp",EDGE,"E74");var subQ2=makeQuery(id+"F2.imprint","INTERSECT",VERTEX,{"disambiguationData":[OD(0.0)],"derivedFrom":[subQ1,subQ0]});Q24=makeQuery(id+"F2.imprint","IMPRINT",FACE,{"disambiguationData":[TD([[makeQuery(id+"F2.imprint","IMPRINT",EDGE,{"disambiguationData":[TD([[subQ2,-1.0]])],"derivedFrom":subQ1}),-1.0]])]});}
            var Q25;
            {var subQ0=sQuery(id+"F2.wireOp",EDGE,"E81.27");var subQ1=sQuery(id+"F2.wireOp",EDGE,"E79");var subQ2=makeQuery(id+"F2.imprint","INTERSECT",VERTEX,{"disambiguationData":[OD(0.0)],"derivedFrom":[subQ1,subQ0]});Q25=makeQuery(id+"F2.imprint","IMPRINT",FACE,{"disambiguationData":[TD([[makeQuery(id+"F2.imprint","IMPRINT",EDGE,{"disambiguationData":[TD([[subQ2,-1.0]])],"derivedFrom":subQ1}),-1.0]])]});}
            var Q26;
            {var subQ0=sQuery(id+"F2.wireOp",EDGE,"E81.26");var subQ1=sQuery(id+"F2.wireOp",EDGE,"E79");var subQ2=makeQuery(id+"F2.imprint","INTERSECT",VERTEX,{"disambiguationData":[OD(0.0)],"derivedFrom":[subQ1,subQ0]});Q26=makeQuery(id+"F2.imprint","IMPRINT",FACE,{"disambiguationData":[TD([[makeQuery(id+"F2.imprint","IMPRINT",EDGE,{"disambiguationData":[TD([[subQ2,-1.0]])],"derivedFrom":subQ1}),-1.0]])]});}
            var Q27;
            {var subQ0=sQuery(id+"F2.wireOp",EDGE,"E81.25");var subQ1=sQuery(id+"F2.wireOp",EDGE,"E79");var subQ2=makeQuery(id+"F2.imprint","INTERSECT",VERTEX,{"disambiguationData":[OD(0.0)],"derivedFrom":[subQ1,subQ0]});Q27=makeQuery(id+"F2.imprint","IMPRINT",FACE,{"disambiguationData":[TD([[makeQuery(id+"F2.imprint","IMPRINT",EDGE,{"disambiguationData":[TD([[subQ2,-1.0]])],"derivedFrom":subQ1}),-1.0]])]});}
            var Q28;
            {var subQ0=sQuery(id+"F2.wireOp",EDGE,"E81.24");var subQ1=sQuery(id+"F2.wireOp",EDGE,"E79");var subQ2=makeQuery(id+"F2.imprint","INTERSECT",VERTEX,{"disambiguationData":[OD(0.0)],"derivedFrom":[subQ1,subQ0]});Q28=makeQuery(id+"F2.imprint","IMPRINT",FACE,{"disambiguationData":[TD([[makeQuery(id+"F2.imprint","IMPRINT",EDGE,{"disambiguationData":[TD([[subQ2,-1.0]])],"derivedFrom":subQ1}),-1.0]])]});}
            extrude(context, id + "F3", {"entities" : qUnion([Q0, Q1, Q2, Q3, Q4, Q5, Q6, Q7, Q8, Q9, Q10, Q11, Q12, Q13, Q14, Q15, Q16, Q17, Q18, Q19, Q20, Q21, Q22, Q23, Q24, Q25, Q26, Q27, Q28]), "depth" : 25.4 * mm});
        }
        {
            var Q0;
            Q0=makeQuery(id+"F3.opExtrude","SWEPT_FACE",FACE,{"disambiguationData":[OSD([sQuery(id+"F2.wireOp",EDGE,"E80.2")])]});
            var sketch = newSketch(context, id + "F4", { "sketchPlane" : qUnion([Q0])});
            skText(sketch, "E82", { "text": "Stern\n", "fontName": "OpenSans-Regular.ttf"});
            const initialGuessF4  = {"E82": [0.17107, 0.00371, 1, 0, 0.01585]};
            skSetInitialGuess(sketch, initialGuessF4);
            skSolve(sketch);
        }
        {
            var Q0;
            Q0 = qSketchRegion(id + "F4", true);
            extrude(context, id + "F5", {"entities" : qUnion([Q0]), "operationType" : NewBodyOperationType.REMOVE, "oppositeDirection" : true, "depth" : 2.54 * mm});
        }
    });
